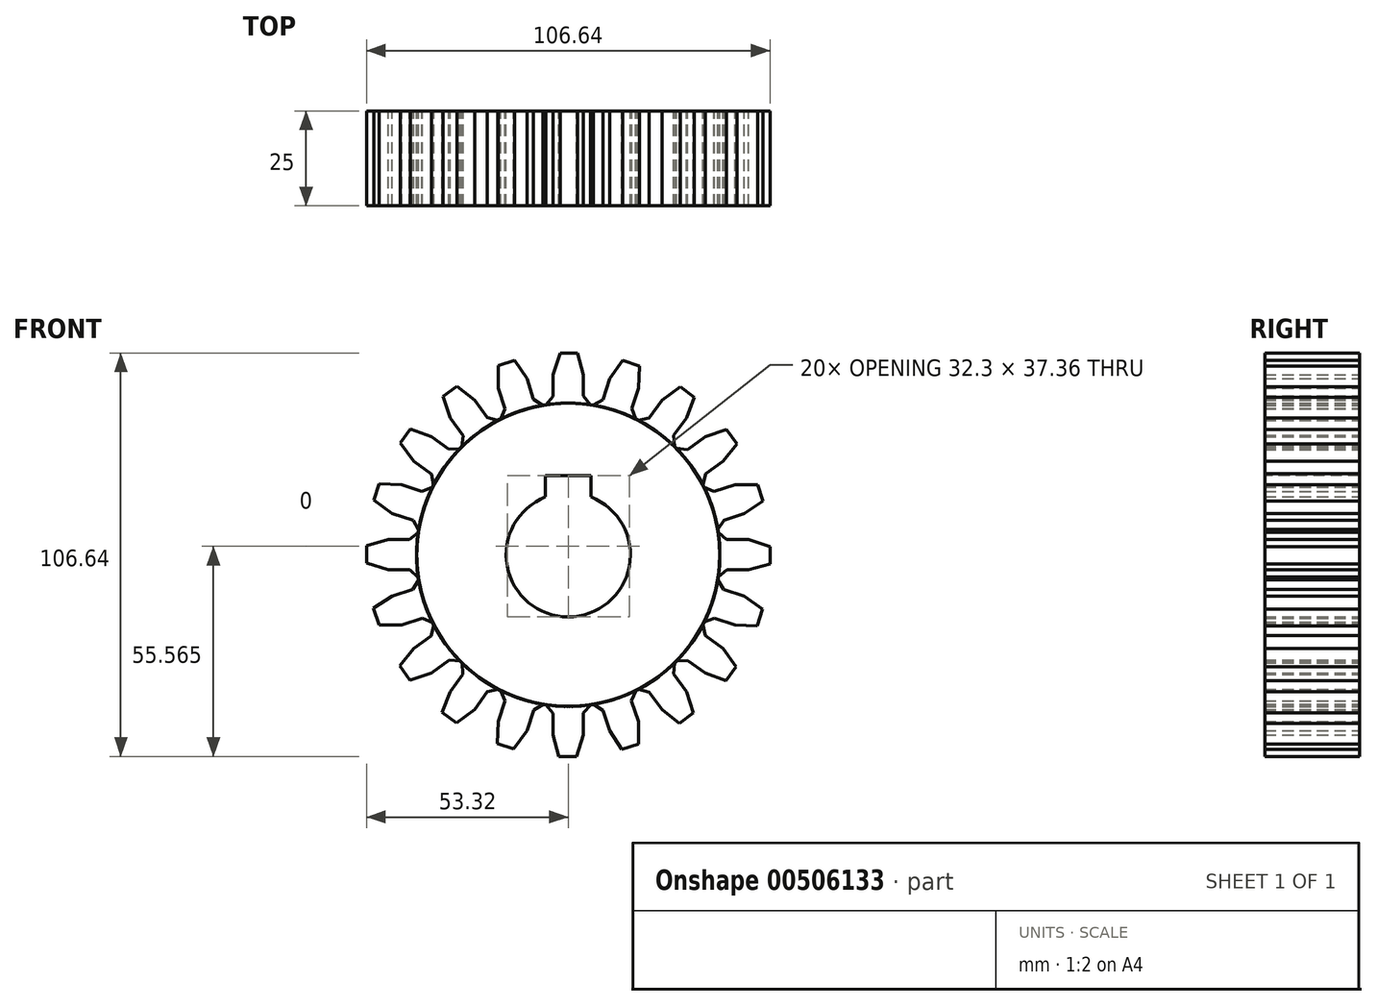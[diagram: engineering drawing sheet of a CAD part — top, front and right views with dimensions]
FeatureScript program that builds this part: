
annotation { "Feature Type Name" : "Feature", "Feature Type Description" : "" }
export const myFeature = defineFeature(function(context is Context, id is Id, definition is map)
    precondition{}
    {
        {
            var Q0;
            Q0=qCreatedBy(makeId("Front.planeOp"),FACE);
            var sketch = newSketch(context, id + "F0", { "sketchPlane" : qUnion([Q0])});
            skArc(sketch, "E0", {"start": v(-5.96, 39.66) * mm, "mid": v(0.05, -40.1) * mm, "end": v(5.86, 39.67) * mm});
            skLineSegment(sketch, "E1.left", {"start": v(4, 41.96) * mm, "end": v(4, 47.63) * mm});
            skLineSegment(sketch, "E1.right", {"start": v(-4, 41.85) * mm, "end": v(-4, 47.63) * mm});
            skPoint(sketch, "E1.middle", {"position": v(0, 30.66) * mm});
            skLineSegment(sketch, "E2", {"start": v(0, 53.32) * mm, "end": v(-2.18, 53.32) * mm});
            skLineSegment(sketch, "E3", {"start": v(0, 53.32) * mm, "end": v(2.44, 53.32) * mm});
            skLineSegment(sketch, "E4", {"start": v(-2.18, 53.32) * mm, "end": v(-4, 47.63) * mm});
            skLineSegment(sketch, "E5", {"start": v(2.44, 53.32) * mm, "end": v(4, 47.63) * mm});
            skPoint(sketch, "E1.bottom.end.orphan", {"position": v(-4, 13.68) * mm});
            skPoint(sketch, "E1.bottom.start.orphan", {"position": v(4, 13.68) * mm});
            skLineSegment(sketch, "E6", {"start": v(-4, 41.85) * mm, "end": v(-5.96, 39.66) * mm});
            skLineSegment(sketch, "E7", {"start": v(4, 41.96) * mm, "end": v(5.86, 39.67) * mm});
            skSolve(sketch);
        }
        {
            var Q0;
            Q0=makeQuery(id+"F0.imprint","IMPRINT",FACE,{"disambiguationData":[TD([[makeQuery(id+"F0.imprint","IMPRINT",EDGE,{"derivedFrom":sQuery(id+"F0.wireOp",EDGE,"E0")}),1.0]])]});
            extrude(context, id + "F1", {"entities" : qUnion([Q0]), "depth" : 25 * mm});
        }
        {
            var Q0;
            Q0=makeQuery(id+"F1.opExtrude","SWEPT_BODY",BODY,{"disambiguationData":[OSD([sQuery(id+"F0.wireOp",EDGE,"E0"),sQuery(id+"F0.wireOp",EDGE,"E1.left"),sQuery(id+"F0.wireOp",EDGE,"E1.right"),sQuery(id+"F0.wireOp",EDGE,"E2"),sQuery(id+"F0.wireOp",EDGE,"E3"),sQuery(id+"F0.wireOp",EDGE,"E4"),sQuery(id+"F0.wireOp",EDGE,"E5"),sQuery(id+"F0.wireOp",EDGE,"E6"),sQuery(id+"F0.wireOp",EDGE,"E7")])]});
            var Q1;
            Q1=makeQuery(id+"F1.opExtrude","CAP_EDGE",EDGE,{"disambiguationData":[OSD([sQuery(id+"F0.wireOp",EDGE,"E0")])],"isStart":false});
            circularPattern(context, id + "F2", {"entities" : qUnion([Q0]), "axis" : qUnion([Q1]), "angle" : 360 * degree, "instanceCount" : 20, "equalSpace" : true});
        }
        {
            var Q0;
            Q0=qCreatedBy(makeId("Front.planeOp"),FACE);
            var sketch = newSketch(context, id + "F3", { "sketchPlane" : qUnion([Q0])});
            skCircle(sketch, "E8", {"center": v(0, 0) * mm, "radius": 16.43 * mm});
            skSolve(sketch);
        }
        {
            var Q0;
            Q0=makeQuery(id+"F3.imprint","IMPRINT",FACE,{"disambiguationData":[TD([[makeQuery(id+"F3.imprint","IMPRINT",EDGE,{"derivedFrom":sQuery(id+"F3.wireOp",EDGE,"E8")}),1.0]])]});
            var Q1;
            Q1=sQuery(id+"F3.wireOp",EDGE,"E8");
            extrude(context, id + "F4", {"entities" : qUnion([Q0]), "operationType" : NewBodyOperationType.REMOVE, "surfaceEntities" : qUnion([Q1]), "endBound" : BoundingType.SYMMETRIC, "depth" : 50 * mm});
        }
        {
            var Q0;
            Q0=qCreatedBy(makeId("Front.planeOp"),FACE);
            var sketch = newSketch(context, id + "F5", { "sketchPlane" : qUnion([Q0])});
            skLineSegment(sketch, "E9.bottom", {"start": v(6, -14.08) * mm, "end": v(-6, -14.08) * mm});
            skLineSegment(sketch, "E9.top", {"start": v(6, 20.92) * mm, "end": v(-6, 20.92) * mm});
            skLineSegment(sketch, "E9.left", {"start": v(6, -14.08) * mm, "end": v(6, 20.92) * mm});
            skLineSegment(sketch, "E9.right", {"start": v(-6, -14.08) * mm, "end": v(-6, 20.92) * mm});
            skPoint(sketch, "E9.middle", {"position": v(0, 3.42) * mm});
            skSolve(sketch);
        }
        {
            var Q0;
            Q0=makeQuery(id+"F5.imprint","IMPRINT",FACE,{"disambiguationData":[TD([[makeQuery(id+"F5.imprint","IMPRINT",EDGE,{"derivedFrom":sQuery(id+"F5.wireOp",EDGE,"E9.bottom")}),-1.0]])]});
            extrude(context, id + "F6", {"entities" : qUnion([Q0]), "operationType" : NewBodyOperationType.REMOVE, "endBound" : BoundingType.SYMMETRIC, "oppositeDirection" : true, "depth" : 50 * mm});
        }
    });
